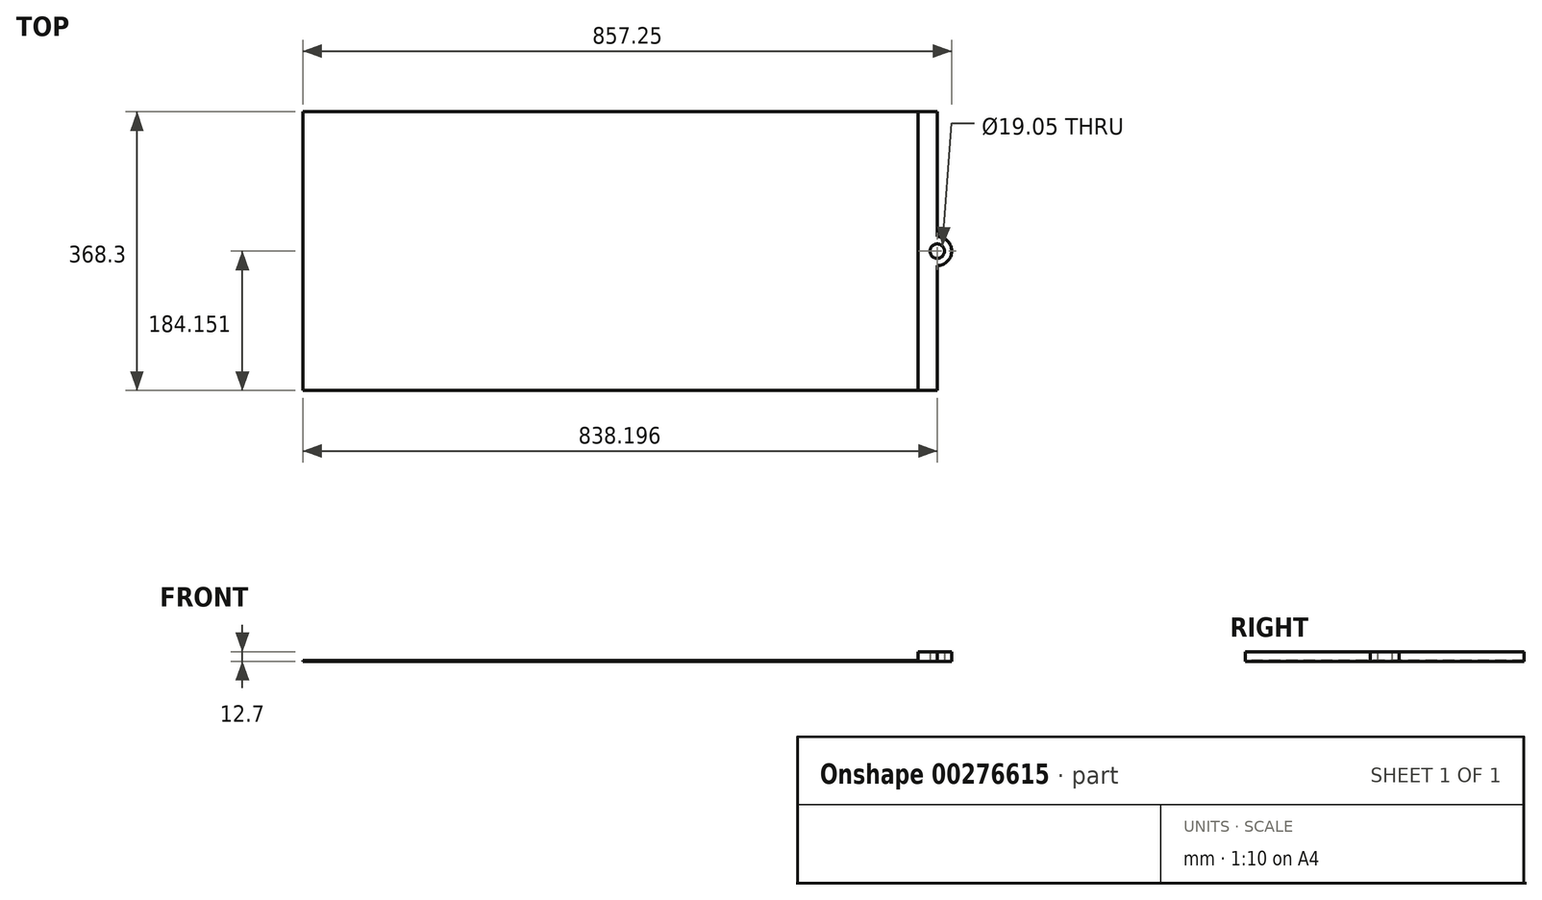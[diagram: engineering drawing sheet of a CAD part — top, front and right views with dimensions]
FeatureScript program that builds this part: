
annotation { "Feature Type Name" : "Feature", "Feature Type Description" : "" }
export const myFeature = defineFeature(function(context is Context, id is Id, definition is map)
    precondition{}
    {
        {
            var Q0;
            Q0=qCreatedBy(makeId("Top.planeOp"),FACE);
            var sketch = newSketch(context, id + "F0", { "sketchPlane" : qUnion([Q0])});
            skLineSegment(sketch, "E0.bottom", {"start": v(-132.33, -102.35) * mm, "end": v(-157.73, -102.35) * mm});
            skLineSegment(sketch, "E0.top", {"start": v(-132.33, 265.95) * mm, "end": v(-157.73, 265.95) * mm});
            skLineSegment(sketch, "E0.left", {"start": v(-132.33, -102.35) * mm, "end": v(-132.33, 62.75) * mm});
            skLineSegment(sketch, "E0.right", {"start": v(-157.73, -102.35) * mm, "end": v(-157.73, 265.95) * mm});
            skPoint(sketch, "E0.middle", {"position": v(-145.03, 81.8) * mm});
            skPoint(sketch, "E0.middle.positionSnap0", {"position": v(-168.2, 81.8) * mm});
            skPoint(sketch, "E0.centerSnap0", {"position": v(-168.2, 81.8) * mm});
            skArc(sketch, "E1", {"start": v(-132.33, 62.75) * mm, "mid": v(-113.28, 81.8) * mm, "end": v(-132.33, 100.85) * mm});
            skCircle(sketch, "E2", {"center": v(-132.33, 81.8) * mm, "radius": 9.53 * mm});
            skLineSegment(sketch, "E3.trimOffspring", {"start": v(-132.33, 100.85) * mm, "end": v(-132.33, 265.95) * mm});
            skSolve(sketch);
        }
        {
            var Q0;
            Q0=makeQuery(id+"F0.imprint","IMPRINT",FACE,{"disambiguationData":[TD([[makeQuery(id+"F0.imprint","IMPRINT",EDGE,{"derivedFrom":sQuery(id+"F0.wireOp",EDGE,"E0.bottom")}),-1.0]])]});
            extrude(context, id + "F1", {"entities" : qUnion([Q0]), "depth" : 12.7 * mm});
        }
        {
            var Q0;
            Q0=qCreatedBy(makeId("Top.planeOp"),FACE);
            var sketch = newSketch(context, id + "F2", { "sketchPlane" : qUnion([Q0])});
            skLineSegment(sketch, "E4.bottom", {"start": v(-970.53, 265.95) * mm, "end": v(-157.73, 265.95) * mm});
            skLineSegment(sketch, "E4.top", {"start": v(-970.53, -102.35) * mm, "end": v(-157.73, -102.35) * mm});
            skLineSegment(sketch, "E4.left", {"start": v(-970.53, 265.95) * mm, "end": v(-970.53, -102.35) * mm});
            skLineSegment(sketch, "E4.right", {"start": v(-157.73, 265.95) * mm, "end": v(-157.73, -102.35) * mm});
            skPoint(sketch, "E4.middle", {"position": v(-564.13, 81.8) * mm});
            skSolve(sketch);
        }
        {
            var Q0;
            Q0=makeQuery(id+"F2.imprint","IMPRINT",FACE,{"disambiguationData":[TD([[makeQuery(id+"F2.imprint","IMPRINT",EDGE,{"derivedFrom":sQuery(id+"F2.wireOp",EDGE,"E4.bottom")}),-1.0]])]});
            extrude(context, id + "F3", {"entities" : qUnion([Q0]), "operationType" : NewBodyOperationType.ADD, "depth" : 1.27 * mm});
        }
    });
